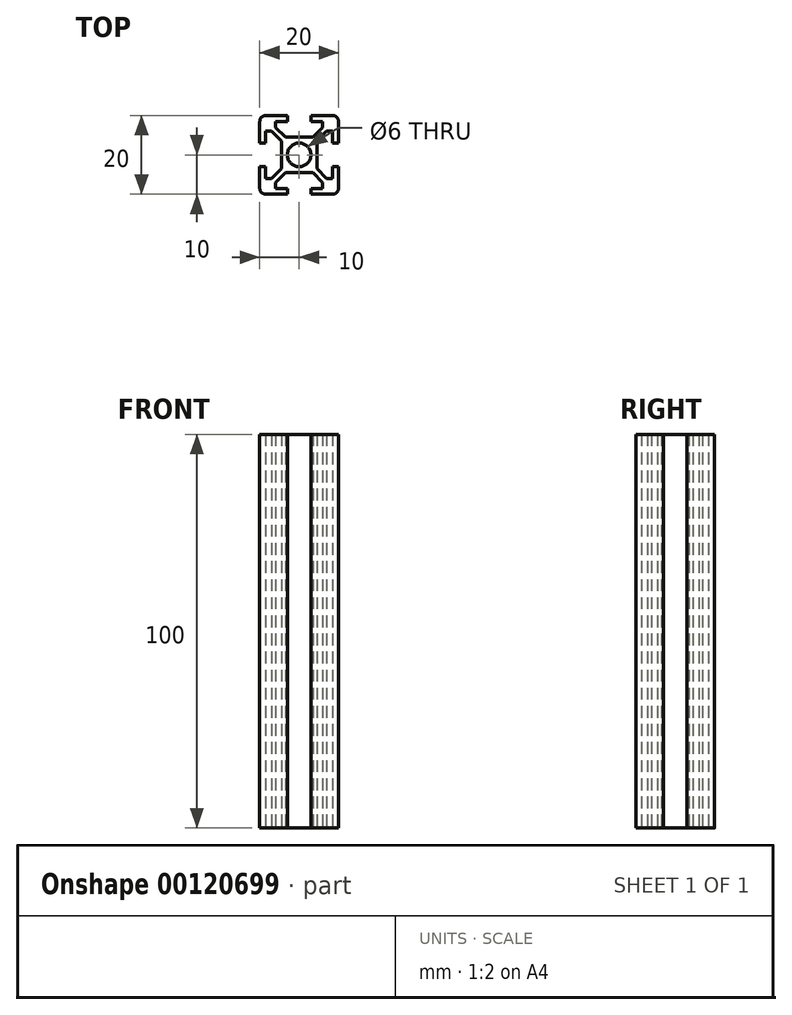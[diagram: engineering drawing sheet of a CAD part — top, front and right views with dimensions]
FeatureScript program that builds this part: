
annotation { "Feature Type Name" : "Feature", "Feature Type Description" : "" }
export const myFeature = defineFeature(function(context is Context, id is Id, definition is map)
    precondition{}
    {
        {
            var Q0;
            Q0=qCreatedBy(makeId("Top.planeOp"),FACE);
            var sketch = newSketch(context, id + "F0", { "sketchPlane" : qUnion([Q0])});
            skLineSegment(sketch, "E0.bottom", {"start": v(1.5, 0) * mm, "end": v(7, 0) * mm});
            skLineSegment(sketch, "E0.top", {"start": v(1.5, 20) * mm, "end": v(7, 20) * mm});
            skLineSegment(sketch, "E0.left", {"start": v(0, 1.5) * mm, "end": v(0, 7) * mm});
            skLineSegment(sketch, "E0.right", {"start": v(20, 1.5) * mm, "end": v(20, 7) * mm});
            skLineSegment(sketch, "E1", {"start": v(10, 25.59) * mm, "end": v(10, -6.26) * mm, "construction": true});
            skPoint(sketch, "E1.startSnap0", {"position": v(10, 20) * mm});
            skLineSegment(sketch, "E2", {"start": v(-5.38, 10) * mm, "end": v(26.16, 10) * mm, "construction": true});
            skPoint(sketch, "E2.startSnap0", {"position": v(0, 10) * mm});
            skPoint(sketch, "E3.visualSharp", {"position": v(20, 20) * mm});
            skArc(sketch, "E3.filletArc", {"start": v(20, 18.5) * mm, "mid": v(19.56, 19.56) * mm, "end": v(18.5, 20) * mm});
            skPoint(sketch, "E4.visualSharp", {"position": v(20, 0) * mm});
            skArc(sketch, "E4.filletArc", {"start": v(18.5, 0) * mm, "mid": v(19.56, 0.44) * mm, "end": v(20, 1.5) * mm});
            skPoint(sketch, "E5.visualSharp", {"position": v(0, 0) * mm});
            skArc(sketch, "E5.filletArc", {"start": v(0, 1.5) * mm, "mid": v(0.44, 0.44) * mm, "end": v(1.5, 0) * mm});
            skPoint(sketch, "E6.visualSharp", {"position": v(0, 20) * mm});
            skArc(sketch, "E6.filletArc", {"start": v(1.5, 20) * mm, "mid": v(0.44, 19.56) * mm, "end": v(0, 18.5) * mm});
            skLineSegment(sketch, "E7", {"start": v(20, 13) * mm, "end": v(18.5, 13) * mm});
            skLineSegment(sketch, "E8", {"start": v(18.5, 13) * mm, "end": v(18.5, 16) * mm});
            skLineSegment(sketch, "E9", {"start": v(18.5, 16) * mm, "end": v(17, 16) * mm});
            skLineSegment(sketch, "E10", {"start": v(17, 16) * mm, "end": v(14.5, 13.5) * mm});
            skLineSegment(sketch, "E11", {"start": v(14.5, 13.5) * mm, "end": v(14.5, 10) * mm});
            skLineSegment(sketch, "E12.MirrorCS", {"start": v(20, 7) * mm, "end": v(18.5, 7) * mm});
            skLineSegment(sketch, "E13.MirrorCS", {"start": v(18.5, 7) * mm, "end": v(18.5, 4) * mm});
            skLineSegment(sketch, "E14.MirrorCS", {"start": v(18.5, 4) * mm, "end": v(17, 4) * mm});
            skLineSegment(sketch, "E15.MirrorCS", {"start": v(14.5, 6.5) * mm, "end": v(14.5, 10) * mm});
            skLineSegment(sketch, "E16.MirrorCS", {"start": v(17, 4) * mm, "end": v(14.5, 6.5) * mm});
            skLineSegment(sketch, "E17.MirrorCS", {"start": v(0, 13) * mm, "end": v(1.5, 13) * mm});
            skLineSegment(sketch, "E18.MirrorCS", {"start": v(1.5, 13) * mm, "end": v(1.5, 16) * mm});
            skLineSegment(sketch, "E19.MirrorCS", {"start": v(1.5, 16) * mm, "end": v(3, 16) * mm});
            skLineSegment(sketch, "E20.MirrorCS", {"start": v(3, 16) * mm, "end": v(5.5, 13.5) * mm});
            skLineSegment(sketch, "E21.MirrorCS", {"start": v(5.5, 13.5) * mm, "end": v(5.5, 10) * mm});
            skLineSegment(sketch, "E22.MirrorCS", {"start": v(5.5, 6.5) * mm, "end": v(5.5, 10) * mm});
            skLineSegment(sketch, "E23.MirrorCS", {"start": v(3, 4) * mm, "end": v(5.5, 6.5) * mm});
            skLineSegment(sketch, "E24.MirrorCS", {"start": v(1.5, 4) * mm, "end": v(3, 4) * mm});
            skLineSegment(sketch, "E25.MirrorCS", {"start": v(1.5, 7) * mm, "end": v(1.5, 4) * mm});
            skLineSegment(sketch, "E26.MirrorCS", {"start": v(0, 7) * mm, "end": v(1.5, 7) * mm});
            skLineSegment(sketch, "E27.1.0", {"start": v(13, 20) * mm, "end": v(13, 18.5) * mm});
            skLineSegment(sketch, "E27.1.1", {"start": v(13, 18.5) * mm, "end": v(16, 18.5) * mm});
            skLineSegment(sketch, "E27.1.2", {"start": v(16, 18.5) * mm, "end": v(16, 17) * mm});
            skLineSegment(sketch, "E27.1.3", {"start": v(16, 17) * mm, "end": v(13.5, 14.5) * mm});
            skLineSegment(sketch, "E27.1.4", {"start": v(13.5, 14.5) * mm, "end": v(10, 14.5) * mm});
            skLineSegment(sketch, "E27.1.5", {"start": v(6.5, 14.5) * mm, "end": v(10, 14.5) * mm});
            skLineSegment(sketch, "E27.1.6", {"start": v(4, 17) * mm, "end": v(6.5, 14.5) * mm});
            skLineSegment(sketch, "E27.1.7", {"start": v(4, 18.5) * mm, "end": v(4, 17) * mm});
            skLineSegment(sketch, "E27.1.8", {"start": v(7, 18.5) * mm, "end": v(4, 18.5) * mm});
            skLineSegment(sketch, "E27.1.9", {"start": v(7, 20) * mm, "end": v(7, 18.5) * mm});
            skPoint(sketch, "E27.center", {"position": v(10, 10) * mm});
            skLineSegment(sketch, "E27.anchor1", {"start": v(10, 10) * mm, "end": v(0, 13) * mm, "construction": true});
            skLineSegment(sketch, "E27.anchor2", {"start": v(10, 10) * mm, "end": v(13, 20) * mm, "construction": true});
            skLineSegment(sketch, "E28.MirrorCS", {"start": v(7, 0) * mm, "end": v(7, 1.5) * mm});
            skLineSegment(sketch, "E29.MirrorCS", {"start": v(7, 1.5) * mm, "end": v(4, 1.5) * mm});
            skLineSegment(sketch, "E30.MirrorCS", {"start": v(4, 1.5) * mm, "end": v(4, 3) * mm});
            skLineSegment(sketch, "E31.MirrorCS", {"start": v(4, 3) * mm, "end": v(6.5, 5.5) * mm});
            skLineSegment(sketch, "E32.MirrorCS", {"start": v(6.5, 5.5) * mm, "end": v(10, 5.5) * mm});
            skLineSegment(sketch, "E33.MirrorCS", {"start": v(13.5, 5.5) * mm, "end": v(10, 5.5) * mm});
            skLineSegment(sketch, "E34.MirrorCS", {"start": v(16, 3) * mm, "end": v(13.5, 5.5) * mm});
            skLineSegment(sketch, "E35.MirrorCS", {"start": v(16, 1.5) * mm, "end": v(16, 3) * mm});
            skLineSegment(sketch, "E36.MirrorCS", {"start": v(13, 1.5) * mm, "end": v(16, 1.5) * mm});
            skLineSegment(sketch, "E37.MirrorCS", {"start": v(13, 0) * mm, "end": v(13, 1.5) * mm});
            skLineSegment(sketch, "E38.trimOffspring", {"start": v(13, 20) * mm, "end": v(18.5, 20) * mm});
            skLineSegment(sketch, "E39.trimOffspring", {"start": v(20, 13) * mm, "end": v(20, 18.5) * mm});
            skLineSegment(sketch, "E40.trimOffspring", {"start": v(13, 0) * mm, "end": v(18.5, 0) * mm});
            skLineSegment(sketch, "E41.trimOffspring", {"start": v(0, 13) * mm, "end": v(0, 18.5) * mm});
            skCircle(sketch, "E42", {"center": v(10, 10) * mm, "radius": 3 * mm});
            skSolve(sketch);
        }
        {
            var Q0;
            Q0=qSketchRegion(id+"F0",true);
            extrude(context, id + "F1", {"entities" : qUnion([Q0]), "depth" : 100 * mm});
        }
    });
